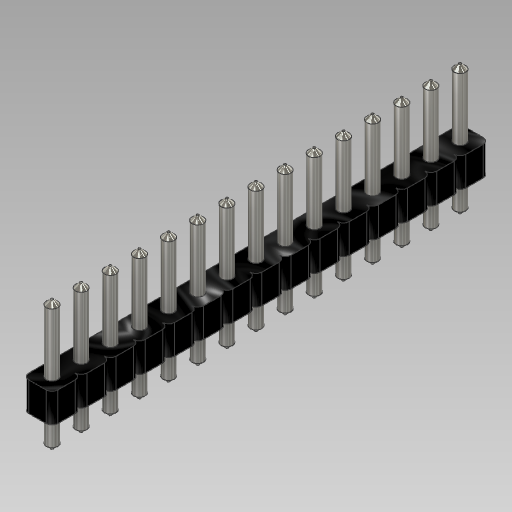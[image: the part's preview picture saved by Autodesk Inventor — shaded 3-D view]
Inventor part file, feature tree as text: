
AUTODESK INVENTOR PART (.ipt)
format: ipt  version: 2020 (Build 240168000, 168)  size: 429,056 bytes
history: native  units: in
note: dims shown in document units (in); Inventor stores cm internally (conversion verified against a paired STEP export)
features: extrude x2, sketch x2, chamfer x1
ambient origin geometry x8: Origin, YZ Plane, XZ Plane, XY Plane, X Axis, Y Axis, Z Axis, Center Point
bodies: Solid1 (feature_tree)
feature tree (5):
  extrude  "Extrusion1"  Depth=0.1in
  extrude  "Extrusion2"  Depth=0.23in TaperAngle=0.0deg
  chamfer  "Chamfer1"  Distance=0.016in Angle=45.0deg
  sketch  "Sketch1"  dims[d0=0.1in d1=0.0in d2=0.04in]
  sketch  "Sketch2"  dims[d3=3.1496in d5=0.1in d6=3.1496in d8=0.1in d11=0.23in d12=0.214in d13=0.0in d14=0.0in d15=0.016in d16=0.125in d17=45.0deg]
